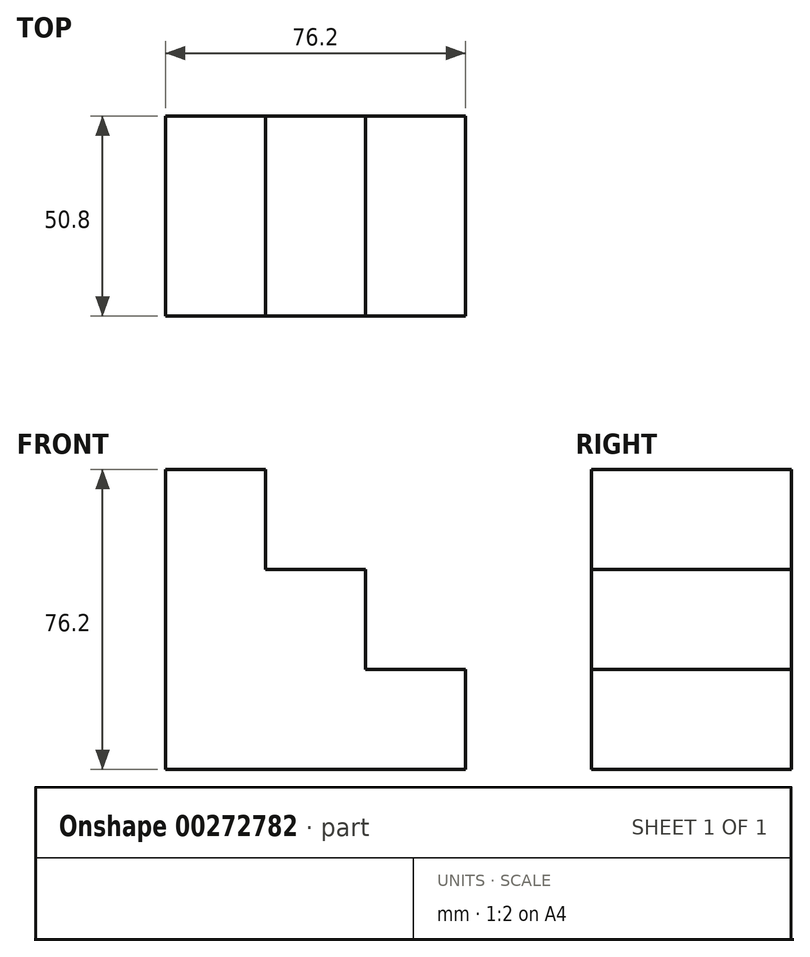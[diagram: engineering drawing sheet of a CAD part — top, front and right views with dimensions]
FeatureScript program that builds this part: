
annotation { "Feature Type Name" : "Feature", "Feature Type Description" : "" }
export const myFeature = defineFeature(function(context is Context, id is Id, definition is map)
    precondition{}
    {
        {
            var Q0;
            Q0=qCreatedBy(makeId("Front.planeOp"),FACE);
            var sketch = newSketch(context, id + "F0", { "sketchPlane" : qUnion([Q0])});
            skLineSegment(sketch, "E0", {"start": v(-64.68, 76.2) * mm, "end": v(-64.68, 0) * mm});
            skLineSegment(sketch, "E1", {"start": v(-64.68, 0) * mm, "end": v(11.52, 0) * mm});
            skLineSegment(sketch, "E2", {"start": v(-64.68, 76.2) * mm, "end": v(-39.28, 76.2) * mm});
            skLineSegment(sketch, "E3", {"start": v(-39.28, 76.2) * mm, "end": v(-39.28, 50.8) * mm});
            skLineSegment(sketch, "E4", {"start": v(-39.28, 50.8) * mm, "end": v(-13.88, 50.8) * mm});
            skLineSegment(sketch, "E5", {"start": v(-13.88, 50.8) * mm, "end": v(-13.88, 25.4) * mm});
            skLineSegment(sketch, "E6", {"start": v(-13.88, 25.4) * mm, "end": v(11.52, 25.4) * mm});
            skLineSegment(sketch, "E7", {"start": v(11.52, 25.4) * mm, "end": v(11.52, 0) * mm});
            skSolve(sketch);
        }
        {
            var Q0;
            Q0 = qSketchRegion(id + "F0", true);
            extrude(context, id + "F1", {"entities" : qUnion([Q0]), "depth" : 50.8 * mm});
        }
    });
